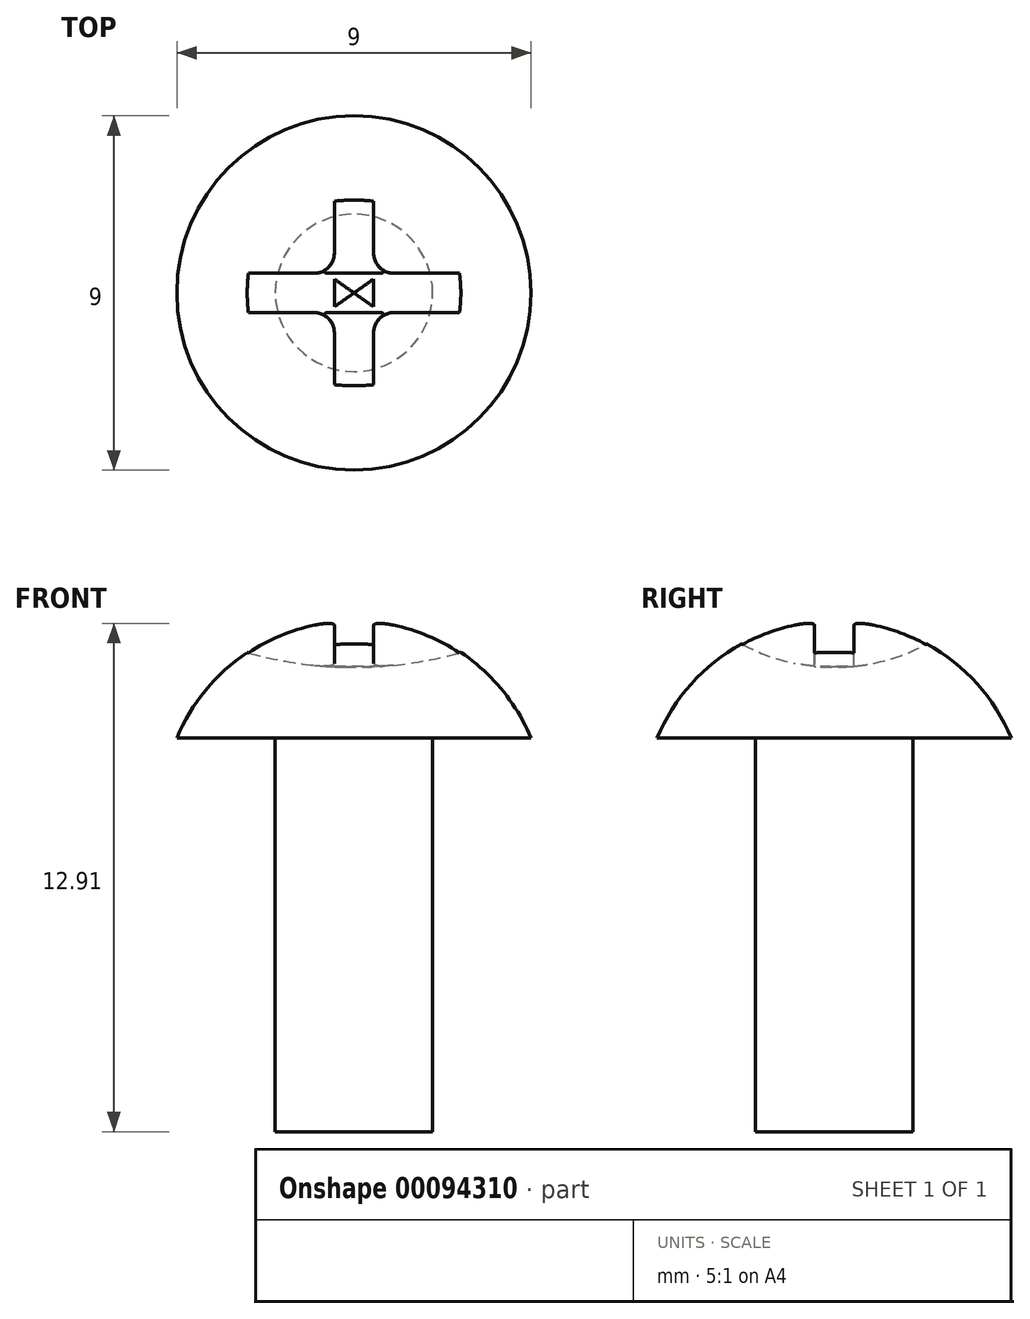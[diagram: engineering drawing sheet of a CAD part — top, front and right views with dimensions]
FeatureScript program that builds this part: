
annotation { "Feature Type Name" : "Feature", "Feature Type Description" : "" }
export const myFeature = defineFeature(function(context is Context, id is Id, definition is map)
    precondition{}
    {
        {
            var Q0;
            Q0=qCreatedBy(makeId("Top.planeOp"),FACE);
            var sketch = newSketch(context, id + "F0", { "sketchPlane" : qUnion([Q0])});
            skCircle(sketch, "E0", {"center": v(0, 0) * mm, "radius": 2 * mm});
            skSolve(sketch);
        }
        {
            var Q0;
            Q0 = qSketchRegion(id + "F0", true);
            extrude(context, id + "F1", {"entities" : qUnion([Q0]), "depth" : 10 * mm});
        }
        {
            var Q0;
            Q0=qCreatedBy(makeId("Front.planeOp"),FACE);
            var sketch = newSketch(context, id + "F2", { "sketchPlane" : qUnion([Q0])});
            skLineSegment(sketch, "E1", {"start": v(0, 10) * mm, "end": v(0, 14) * mm, "construction": true});
            skPoint(sketch, "E2", {"position": v(0, 10) * mm});
            skLineSegment(sketch, "E3", {"start": v(0, 10) * mm, "end": v(0, 8.08) * mm, "construction": true});
            skLineSegment(sketch, "E4", {"start": v(4.5, 10) * mm, "end": v(0, 10) * mm});
            skLineSegment(sketch, "E5", {"start": v(0, 14.5) * mm, "end": v(0, 10) * mm});
            skPoint(sketch, "E6", {"position": v(0, 13) * mm});
            skArc(sketch, "E7", {"start": v(4.5, 10) * mm, "mid": v(2.7, 12.18) * mm, "end": v(0, 13) * mm});
            skLineSegment(sketch, "E8", {"start": v(0, 13) * mm, "end": v(0, 10) * mm});
            skPoint(sketch, "E9.MirrorCS.start.orphan", {"position": v(-4.5, 10) * mm});
            skSolve(sketch);
        }
        {
            var Q0;
            Q0=makeQuery(id+"F2.imprint","IMPRINT",FACE,{"disambiguationData":[TD([[makeQuery(id+"F2.imprint","IMPRINT",EDGE,{"derivedFrom":sQuery(id+"F2.wireOp",EDGE,"E4")}),-1.0]])]});
            var Q1;
            Q1=sQuery(id+"F2.wireOp",EDGE,"E5");
            revolve(context, id + "F3", {"operationType" : NewBodyOperationType.ADD, "entities" : qUnion([Q0]), "axis" : qUnion([Q1]), "revolveType" : RevolveType.FULL});
        }
        {
            var Q0;
            Q0=qCreatedBy(makeId("Front.planeOp"),FACE);
            var sketch = newSketch(context, id + "F4", { "sketchPlane" : qUnion([Q0])});
            skArc(sketch, "E10", {"start": v(2.72, 12.18) * mm, "mid": v(0, 13) * mm, "end": v(-2.72, 12.18) * mm});
            skArc(sketch, "E11", {"start": v(-2.72, 12.18) * mm, "mid": v(0, 11.8) * mm, "end": v(2.72, 12.18) * mm});
            skSolve(sketch);
        }
        {
            var Q0;
            Q0 = qSketchRegion(id + "F4", true);
            extrude(context, id + "F5", {"entities" : qUnion([Q0]), "operationType" : NewBodyOperationType.REMOVE, "endBound" : BoundingType.SYMMETRIC, "oppositeDirection" : true, "depth" : 1 * mm});
        }
        {
            var Q0;
            Q0=qCreatedBy(makeId("Right.planeOp"),FACE);
            var sketch = newSketch(context, id + "F6", { "sketchPlane" : qUnion([Q0])});
            skArc(sketch, "E12", {"start": v(2.36, 12.4) * mm, "mid": v(0, 13) * mm, "end": v(-2.36, 12.4) * mm});
            skArc(sketch, "E13", {"start": v(-2.36, 12.4) * mm, "mid": v(0, 11.8) * mm, "end": v(2.36, 12.4) * mm});
            skSolve(sketch);
        }
        {
            var Q0;
            Q0 = qSketchRegion(id + "F6", true);
            extrude(context, id + "F7", {"entities" : qUnion([Q0]), "operationType" : NewBodyOperationType.REMOVE, "endBound" : BoundingType.SYMMETRIC, "depth" : 1 * mm});
        }
        {
            var Q0;
            Q0=makeQuery(id+"F7.boolean.opBoolean","INTERSECT",EDGE,{"derivedFrom":[makeQuery(id+"F5.boolean.opBoolean","COPY",FACE,{"derivedFrom":makeQuery(id+"F5.opExtrude","CAP_FACE",FACE,{"disambiguationData":[OSD([sQuery(id+"F4.wireOp",EDGE,"E10"),sQuery(id+"F4.wireOp",EDGE,"E11")])],"isStart":true})}),makeQuery(id+"F7.opExtrude","CAP_FACE",FACE,{"disambiguationData":[OSD([sQuery(id+"F6.wireOp",EDGE,"E12"),sQuery(id+"F6.wireOp",EDGE,"E13")])],"isStart":false})]});
            var Q1;
            Q1=makeQuery(id+"F7.boolean.opBoolean","INTERSECT",EDGE,{"derivedFrom":[makeQuery(id+"F5.boolean.opBoolean","COPY",FACE,{"derivedFrom":makeQuery(id+"F5.opExtrude","CAP_FACE",FACE,{"disambiguationData":[OSD([sQuery(id+"F4.wireOp",EDGE,"E10"),sQuery(id+"F4.wireOp",EDGE,"E11")])],"isStart":true})}),makeQuery(id+"F7.opExtrude","CAP_FACE",FACE,{"disambiguationData":[OSD([sQuery(id+"F6.wireOp",EDGE,"E12"),sQuery(id+"F6.wireOp",EDGE,"E13")])],"isStart":true})]});
            var Q2;
            Q2=makeQuery(id+"F7.boolean.opBoolean","INTERSECT",EDGE,{"derivedFrom":[makeQuery(id+"F5.boolean.opBoolean","COPY",FACE,{"derivedFrom":makeQuery(id+"F5.opExtrude","CAP_FACE",FACE,{"disambiguationData":[OSD([sQuery(id+"F4.wireOp",EDGE,"E10"),sQuery(id+"F4.wireOp",EDGE,"E11")])],"isStart":false})}),makeQuery(id+"F7.opExtrude","CAP_FACE",FACE,{"disambiguationData":[OSD([sQuery(id+"F6.wireOp",EDGE,"E12"),sQuery(id+"F6.wireOp",EDGE,"E13")])],"isStart":true})]});
            var Q3;
            Q3=makeQuery(id+"F7.boolean.opBoolean","INTERSECT",EDGE,{"derivedFrom":[makeQuery(id+"F5.boolean.opBoolean","COPY",FACE,{"derivedFrom":makeQuery(id+"F5.opExtrude","CAP_FACE",FACE,{"disambiguationData":[OSD([sQuery(id+"F4.wireOp",EDGE,"E10"),sQuery(id+"F4.wireOp",EDGE,"E11")])],"isStart":false})}),makeQuery(id+"F7.opExtrude","CAP_FACE",FACE,{"disambiguationData":[OSD([sQuery(id+"F6.wireOp",EDGE,"E12"),sQuery(id+"F6.wireOp",EDGE,"E13")])],"isStart":false})]});
            fillet(context, id + "F8", {"entities" : qUnion([Q0, Q1, Q2, Q3]), "radius" : 0.5 * mm, "tangentPropagation" : true, "allowEdgeOverflow" : false});
        }
    });
